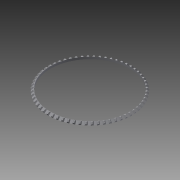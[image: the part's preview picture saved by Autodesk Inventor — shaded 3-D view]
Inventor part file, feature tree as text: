
AUTODESK INVENTOR PART (.ipt)
format: ipt  version: 2015 (Build 190159000, 159)  size: 582,656 bytes
history: native  units: in
note: dims shown in document units (in); Inventor stores cm internally (conversion verified against a paired STEP export)
features: extrude x3, sketch x3, pattern_circular x1
ambient origin geometry x8: Origin, YZ Plane, XZ Plane, XY Plane, X Axis, Y Axis, Z Axis, Center Point
bodies: Body1 (feature_tree)
feature tree (7):
  extrude  "Extrusion2"  Depth=3.8in
  extrude  "Extrusion3"  Depth=3.6in
  extrude  "Extrusion4"  Depth=0.05in
  pattern_circular  "Circular Pattern1"  Count=60 Angle=360.0deg
  sketch  "Sketch2"  dims[d1=1.875in d11=3.8in]
  sketch  "Sketch3"  dims[d12=3.0in d13=-0.3092in d14=3.6in]
  sketch  "Sketch4"  dims[d15=3.0in d16=0.0in d17=0.05in d18=-0.2061in d19=23.622in d20=360.0deg]
